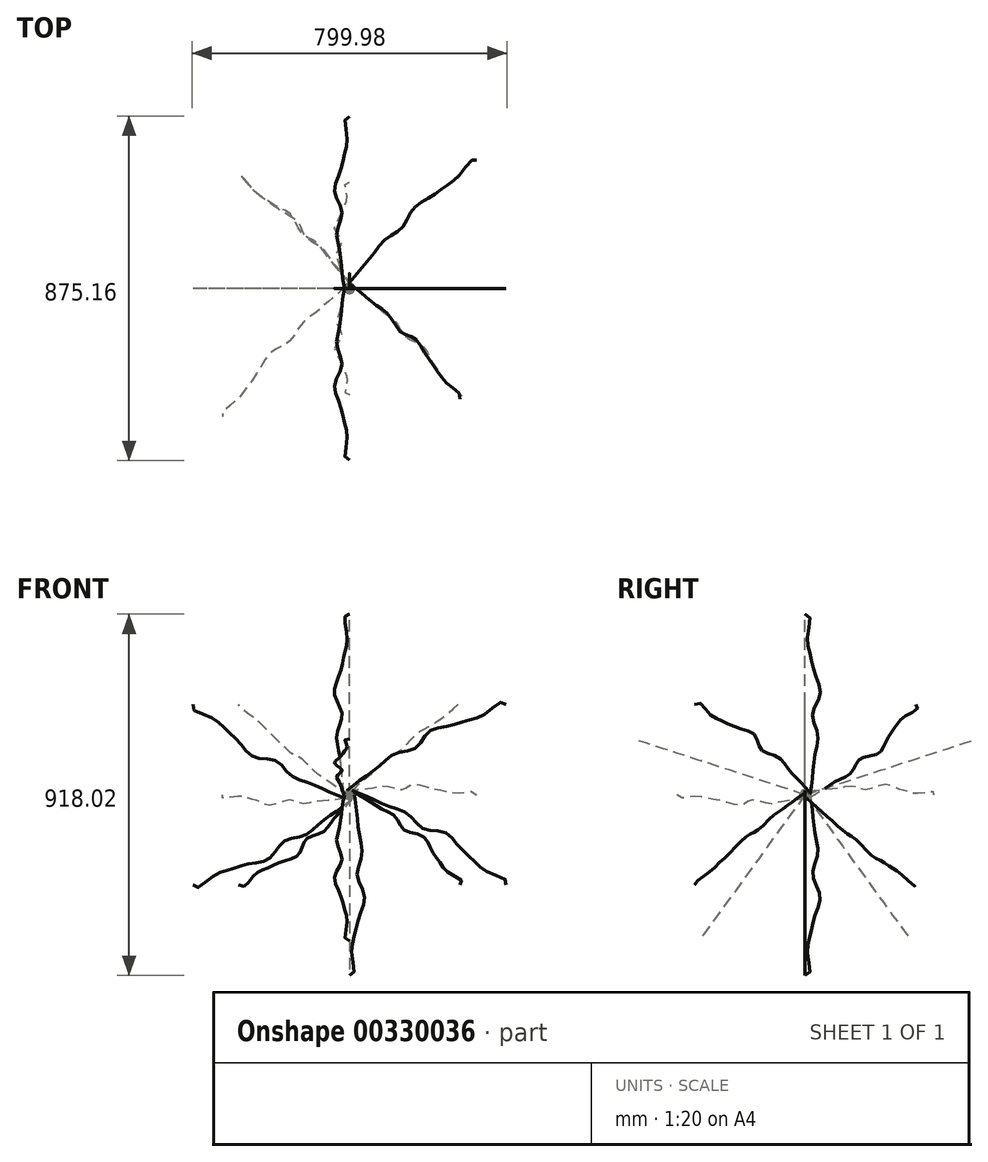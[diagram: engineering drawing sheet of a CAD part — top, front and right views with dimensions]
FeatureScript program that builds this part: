
annotation { "Feature Type Name" : "Feature", "Feature Type Description" : "" }
export const myFeature = defineFeature(function(context is Context, id is Id, definition is map)
    precondition{}
    {
        {
            var Q0;
            Q0=qCreatedBy(makeId("Top.planeOp"),FACE);
            cPlane(context, id + "F0", {"entities" : qUnion([Q0]), "cplaneType" : CPlaneType.OFFSET, "offset" : 46.48 * mm, "width" : 152.4 * mm, "height" : 152.4 * mm});
        }
        {
            var Q0;
            Q0=qCreatedBy(id+"F0.planeOp",FACE);
            cPlane(context, id + "F1", {"entities" : qUnion([Q0]), "cplaneType" : CPlaneType.OFFSET, "offset" : 56.64 * mm, "width" : 152.4 * mm, "height" : 152.4 * mm});
        }
        {
            var Q0;
            Q0=qCreatedBy(id+"F1.planeOp",FACE);
            cPlane(context, id + "F2", {"entities" : qUnion([Q0]), "cplaneType" : CPlaneType.OFFSET, "offset" : 50.8 * mm, "width" : 152.4 * mm, "height" : 152.4 * mm});
        }
        {
            var Q0;
            Q0=qCreatedBy(id+"F2.planeOp",FACE);
            cPlane(context, id + "F3", {"entities" : qUnion([Q0]), "cplaneType" : CPlaneType.OFFSET, "offset" : 50.8 * mm, "width" : 152.4 * mm, "height" : 152.4 * mm});
        }
        {
            var Q0;
            Q0=qCreatedBy(makeId("Top.planeOp"),FACE);
            var sketch = newSketch(context, id + "F4", { "sketchPlane" : qUnion([Q0])});
            skCircle(sketch, "E0", {"center": v(0, 0) * mm, "radius": 12.7 * mm});
            skSolve(sketch);
        }
        {
            var Q0;
            Q0=qCreatedBy(id+"F0.planeOp",FACE);
            var sketch = newSketch(context, id + "F5", { "sketchPlane" : qUnion([Q0])});
            skCircle(sketch, "E1", {"center": v(0, 0) * mm, "radius": 19.05 * mm});
            skSolve(sketch);
        }
        {
            var Q0;
            Q0=qCreatedBy(id+"F1.planeOp",FACE);
            var sketch = newSketch(context, id + "F6", { "sketchPlane" : qUnion([Q0])});
            skCircle(sketch, "E2", {"center": v(0, 0) * mm, "radius": 25.4 * mm});
            skSolve(sketch);
        }
        {
            var Q0;
            Q0=qCreatedBy(id+"F3.planeOp",FACE);
            cPlane(context, id + "F7", {"entities" : qUnion([Q0]), "cplaneType" : CPlaneType.OFFSET, "offset" : 50.8 * mm, "width" : 152.4 * mm, "height" : 152.4 * mm});
        }
        {
            var Q0;
            Q0=qCreatedBy(id+"F7.planeOp",FACE);
            cPlane(context, id + "F8", {"entities" : qUnion([Q0]), "cplaneType" : CPlaneType.OFFSET, "offset" : 50.8 * mm, "width" : 152.4 * mm, "height" : 152.4 * mm});
        }
        {
            var Q0;
            Q0=qCreatedBy(id+"F8.planeOp",FACE);
            cPlane(context, id + "F9", {"entities" : qUnion([Q0]), "cplaneType" : CPlaneType.OFFSET, "offset" : 50.8 * mm, "width" : 152.4 * mm, "height" : 152.4 * mm});
        }
        {
            var Q0;
            Q0=qCreatedBy(id+"F2.planeOp",FACE);
            var sketch = newSketch(context, id + "F10", { "sketchPlane" : qUnion([Q0])});
            skCircle(sketch, "E3", {"center": v(0, 0) * mm, "radius": 31.75 * mm});
            skSolve(sketch);
        }
        {
            var Q0;
            Q0=qCreatedBy(id+"F3.planeOp",FACE);
            var sketch = newSketch(context, id + "F11", { "sketchPlane" : qUnion([Q0])});
            skCircle(sketch, "E4", {"center": v(0, 0) * mm, "radius": 19.05 * mm});
            skSolve(sketch);
        }
        {
            var Q0;
            Q0=qCreatedBy(id+"F7.planeOp",FACE);
            var sketch = newSketch(context, id + "F12", { "sketchPlane" : qUnion([Q0])});
            skCircle(sketch, "E5", {"center": v(0, 0) * mm, "radius": 38.1 * mm});
            skSolve(sketch);
        }
        {
            var Q0;
            Q0=qCreatedBy(id+"F8.planeOp",FACE);
            var sketch = newSketch(context, id + "F13", { "sketchPlane" : qUnion([Q0])});
            skCircle(sketch, "E6", {"center": v(0, 0) * mm, "radius": 25.4 * mm});
            skSolve(sketch);
        }
        {
            var Q0;
            Q0=qCreatedBy(id+"F9.planeOp",FACE);
            var sketch = newSketch(context, id + "F14", { "sketchPlane" : qUnion([Q0])});
            skCircle(sketch, "E7", {"center": v(0, 0) * mm, "radius": 12.7 * mm});
            skSolve(sketch);
        }
        {
            var Q0;
            Q0=qCreatedBy(id+"F9.planeOp",FACE);
            cPlane(context, id + "F15", {"entities" : qUnion([Q0]), "cplaneType" : CPlaneType.OFFSET, "offset" : 50.8 * mm, "width" : 152.4 * mm, "height" : 152.4 * mm});
        }
        {
            var Q0;
            Q0=qCreatedBy(id+"F15.planeOp",FACE);
            cPlane(context, id + "F16", {"entities" : qUnion([Q0]), "cplaneType" : CPlaneType.OFFSET, "offset" : 50.8 * mm, "width" : 152.4 * mm, "height" : 152.4 * mm});
        }
        {
            var Q0;
            Q0=qCreatedBy(id+"F15.planeOp",FACE);
            var sketch = newSketch(context, id + "F17", { "sketchPlane" : qUnion([Q0])});
            skCircle(sketch, "E8", {"center": v(0, 0) * mm, "radius": 6.35 * mm});
            skSolve(sketch);
        }
        {
            var Q0;
            Q0=qCreatedBy(id+"F16.planeOp",FACE);
            var sketch = newSketch(context, id + "F18", { "sketchPlane" : qUnion([Q0])});
            skCircle(sketch, "E9", {"center": v(0, 0) * mm, "radius": 3.18 * mm});
            skSolve(sketch);
        }
        {
            var Q0;
            Q0=makeQuery(id+"F4.imprint","IMPRINT",FACE,{"disambiguationData":[TD([[makeQuery(id+"F4.imprint","IMPRINT",EDGE,{"derivedFrom":sQuery(id+"F4.wireOp",EDGE,"E0")}),1.0]])]});
            var Q1;
            Q1=makeQuery(id+"F5.imprint","IMPRINT",FACE,{"disambiguationData":[TD([[makeQuery(id+"F5.imprint","IMPRINT",EDGE,{"derivedFrom":sQuery(id+"F5.wireOp",EDGE,"E1")}),1.0]])]});
            var Q2;
            Q2=makeQuery(id+"F6.imprint","IMPRINT",FACE,{"disambiguationData":[TD([[makeQuery(id+"F6.imprint","IMPRINT",EDGE,{"derivedFrom":sQuery(id+"F6.wireOp",EDGE,"E2")}),1.0]])]});
            var Q3;
            Q3=makeQuery(id+"F10.imprint","IMPRINT",FACE,{"disambiguationData":[TD([[makeQuery(id+"F10.imprint","IMPRINT",EDGE,{"derivedFrom":sQuery(id+"F10.wireOp",EDGE,"E3")}),1.0]])]});
            var Q4;
            Q4=makeQuery(id+"F11.imprint","IMPRINT",FACE,{"disambiguationData":[TD([[makeQuery(id+"F11.imprint","IMPRINT",EDGE,{"derivedFrom":sQuery(id+"F11.wireOp",EDGE,"E4")}),1.0]])]});
            var Q5;
            Q5=makeQuery(id+"F12.imprint","IMPRINT",FACE,{"disambiguationData":[TD([[makeQuery(id+"F12.imprint","IMPRINT",EDGE,{"derivedFrom":sQuery(id+"F12.wireOp",EDGE,"E5")}),1.0]])]});
            var Q6;
            Q6=makeQuery(id+"F13.imprint","IMPRINT",FACE,{"disambiguationData":[TD([[makeQuery(id+"F13.imprint","IMPRINT",EDGE,{"derivedFrom":sQuery(id+"F13.wireOp",EDGE,"E6")}),1.0]])]});
            var Q7;
            Q7=makeQuery(id+"F14.imprint","IMPRINT",FACE,{"disambiguationData":[TD([[makeQuery(id+"F14.imprint","IMPRINT",EDGE,{"derivedFrom":sQuery(id+"F14.wireOp",EDGE,"E7")}),1.0]])]});
            var Q8;
            Q8=makeQuery(id+"F17.imprint","IMPRINT",FACE,{"disambiguationData":[TD([[makeQuery(id+"F17.imprint","IMPRINT",EDGE,{"derivedFrom":sQuery(id+"F17.wireOp",EDGE,"E8")}),1.0]])]});
            var Q9;
            Q9=makeQuery(id+"F18.imprint","IMPRINT",FACE,{"disambiguationData":[TD([[makeQuery(id+"F18.imprint","IMPRINT",EDGE,{"derivedFrom":sQuery(id+"F18.wireOp",EDGE,"E9")}),1.0]])]});
            var Q10;
            Q10=sQuery(id+"F18.wireOp",VERTEX,"E9.center");
            loft(context, id + "F19", {"sheetProfilesArray" : [{ "sheetProfileEntities" : qUnion([Q0]) }, { "sheetProfileEntities" : qUnion([Q1]) }, { "sheetProfileEntities" : qUnion([Q2]) }, { "sheetProfileEntities" : qUnion([Q3]) }, { "sheetProfileEntities" : qUnion([Q4]) }, { "sheetProfileEntities" : qUnion([Q5]) }, { "sheetProfileEntities" : qUnion([Q6]) }, { "sheetProfileEntities" : qUnion([Q7]) }, { "sheetProfileEntities" : qUnion([Q8]) }, { "sheetProfileEntities" : qUnion([Q9]) }, { "sheetProfileEntities" : qUnion([Q10]) }]});
        }
        {
            var Q0;
            Q0=qCreatedBy(id+"F16.planeOp",FACE);
            cPlane(context, id + "F20", {"entities" : qUnion([Q0]), "cplaneType" : CPlaneType.OFFSET, "offset" : 25.4 * mm, "width" : 152.4 * mm, "height" : 152.4 * mm});
        }
        {
            var Q0;
            Q0=qCreatedBy(makeId("Top.planeOp"),FACE);
            var sketch = newSketch(context, id + "F21", { "sketchPlane" : qUnion([Q0])});
            skLineSegment(sketch, "E10", {"start": v(76.24, 0) * mm, "end": v(-76.24, 0) * mm, "construction": true});
            skSolve(sketch);
        }
        {
            var Q0;
            Q0=makeQuery(id+"F19.opLoft","SWEPT_BODY",BODY,{"disambiguationData":[OSD([makeQuery(id+"F4.imprint","IMPRINT",FACE,{"disambiguationData":[TD([[makeQuery(id+"F4.imprint","IMPRINT",EDGE,{"derivedFrom":sQuery(id+"F4.wireOp",EDGE,"E0")}),1.0]])]}),sQuery(id+"F5.wireOp",EDGE,"E1"),sQuery(id+"F6.wireOp",EDGE,"E2"),sQuery(id+"F10.wireOp",EDGE,"E3"),sQuery(id+"F11.wireOp",EDGE,"E4"),sQuery(id+"F12.wireOp",EDGE,"E5"),sQuery(id+"F13.wireOp",EDGE,"E6"),sQuery(id+"F14.wireOp",EDGE,"E7"),sQuery(id+"F17.wireOp",EDGE,"E8"),sQuery(id+"F18.wireOp",VERTEX,"E9.center"),sQuery(id+"F18.wireOp",EDGE,"E9")])]});
            var Q1;
            Q1=sQuery(id+"F21.wireOp",EDGE,"E10");
            circularPattern(context, id + "F22", {"entities" : qUnion([Q0]), "axis" : qUnion([Q1]), "angle" : 360 * degree, "instanceCount" : 5, "equalSpace" : true});
        }
        {
            var Q0;
            Q0=qCreatedBy(makeId("Right.planeOp"),FACE);
            var sketch = newSketch(context, id + "F23", { "sketchPlane" : qUnion([Q0])});
            skLineSegment(sketch, "E11", {"start": v(-76.33, -0.12) * mm, "end": v(76.33, -0.12) * mm, "construction": true});
            skSolve(sketch);
        }
        {
            var Q0;
            Q0=makeQuery(id+"F19.opLoft","SWEPT_BODY",BODY,{"disambiguationData":[OSD([makeQuery(id+"F4.imprint","IMPRINT",FACE,{"disambiguationData":[TD([[makeQuery(id+"F4.imprint","IMPRINT",EDGE,{"derivedFrom":sQuery(id+"F4.wireOp",EDGE,"E0")}),1.0]])]}),sQuery(id+"F5.wireOp",EDGE,"E1"),sQuery(id+"F6.wireOp",EDGE,"E2"),sQuery(id+"F10.wireOp",EDGE,"E3"),sQuery(id+"F11.wireOp",EDGE,"E4"),sQuery(id+"F12.wireOp",EDGE,"E5"),sQuery(id+"F13.wireOp",EDGE,"E6"),sQuery(id+"F14.wireOp",EDGE,"E7"),sQuery(id+"F17.wireOp",EDGE,"E8"),sQuery(id+"F18.wireOp",VERTEX,"E9.center"),sQuery(id+"F18.wireOp",EDGE,"E9")])]});
            var Q1;
            Q1=sQuery(id+"F23.wireOp",EDGE,"E11");
            circularPattern(context, id + "F24", {"entities" : qUnion([Q0]), "axis" : qUnion([Q1]), "angle" : 360 * degree, "instanceCount" : 6, "equalSpace" : true});
        }
        {
            var Q0;
            Q0=qCreatedBy(makeId("Top.planeOp"),FACE);
            var sketch = newSketch(context, id + "F25", { "sketchPlane" : qUnion([Q0])});
            skLineSegment(sketch, "E12", {"start": v(76.1, 76.3) * mm, "end": v(-70.61, -70.68) * mm, "construction": true});
            skSolve(sketch);
        }
        {
            var Q0;
            Q0=makeQuery(id+"F24.opPattern","COPY",BODY,{"derivedFrom":makeQuery(id+"F19.opLoft","SWEPT_BODY",BODY,{"disambiguationData":[OSD([makeQuery(id+"F4.imprint","IMPRINT",FACE,{"disambiguationData":[TD([[makeQuery(id+"F4.imprint","IMPRINT",EDGE,{"derivedFrom":sQuery(id+"F4.wireOp",EDGE,"E0")}),1.0]])]}),sQuery(id+"F5.wireOp",EDGE,"E1"),sQuery(id+"F6.wireOp",EDGE,"E2"),sQuery(id+"F10.wireOp",EDGE,"E3"),sQuery(id+"F11.wireOp",EDGE,"E4"),sQuery(id+"F12.wireOp",EDGE,"E5"),sQuery(id+"F13.wireOp",EDGE,"E6"),sQuery(id+"F14.wireOp",EDGE,"E7"),sQuery(id+"F17.wireOp",EDGE,"E8"),sQuery(id+"F18.wireOp",VERTEX,"E9.center"),sQuery(id+"F18.wireOp",EDGE,"E9")])]}),"instanceName":"3"});
            var Q1;
            Q1=sQuery(id+"F25.wireOp",EDGE,"E12");
            circularPattern(context, id + "F26", {"entities" : qUnion([Q0]), "axis" : qUnion([Q1]), "angle" : 360 * degree, "instanceCount" : 6, "equalSpace" : true});
        }
        {
            var Q0;
            Q0=qCreatedBy(makeId("Top.planeOp"),FACE);
            var sketch = newSketch(context, id + "F27", { "sketchPlane" : qUnion([Q0])});
            skLineSegment(sketch, "E13", {"start": v(0, 0) * mm, "end": v(72.01, -71.32) * mm, "construction": true});
            skSolve(sketch);
        }
        {
            var Q0;
            Q0=makeQuery(id+"F19.opLoft","SWEPT_BODY",BODY,{"disambiguationData":[OSD([makeQuery(id+"F4.imprint","IMPRINT",FACE,{"disambiguationData":[TD([[makeQuery(id+"F4.imprint","IMPRINT",EDGE,{"derivedFrom":sQuery(id+"F4.wireOp",EDGE,"E0")}),1.0]])]}),sQuery(id+"F5.wireOp",EDGE,"E1"),sQuery(id+"F6.wireOp",EDGE,"E2"),sQuery(id+"F10.wireOp",EDGE,"E3"),sQuery(id+"F11.wireOp",EDGE,"E4"),sQuery(id+"F12.wireOp",EDGE,"E5"),sQuery(id+"F13.wireOp",EDGE,"E6"),sQuery(id+"F14.wireOp",EDGE,"E7"),sQuery(id+"F17.wireOp",EDGE,"E8"),sQuery(id+"F18.wireOp",VERTEX,"E9.center"),sQuery(id+"F18.wireOp",EDGE,"E9")])]});
            var Q1;
            Q1=sQuery(id+"F27.wireOp",EDGE,"E13");
            circularPattern(context, id + "F28", {"entities" : qUnion([Q0]), "axis" : qUnion([Q1]), "angle" : 360 * degree, "instanceCount" : 4, "equalSpace" : true});
        }
    });
